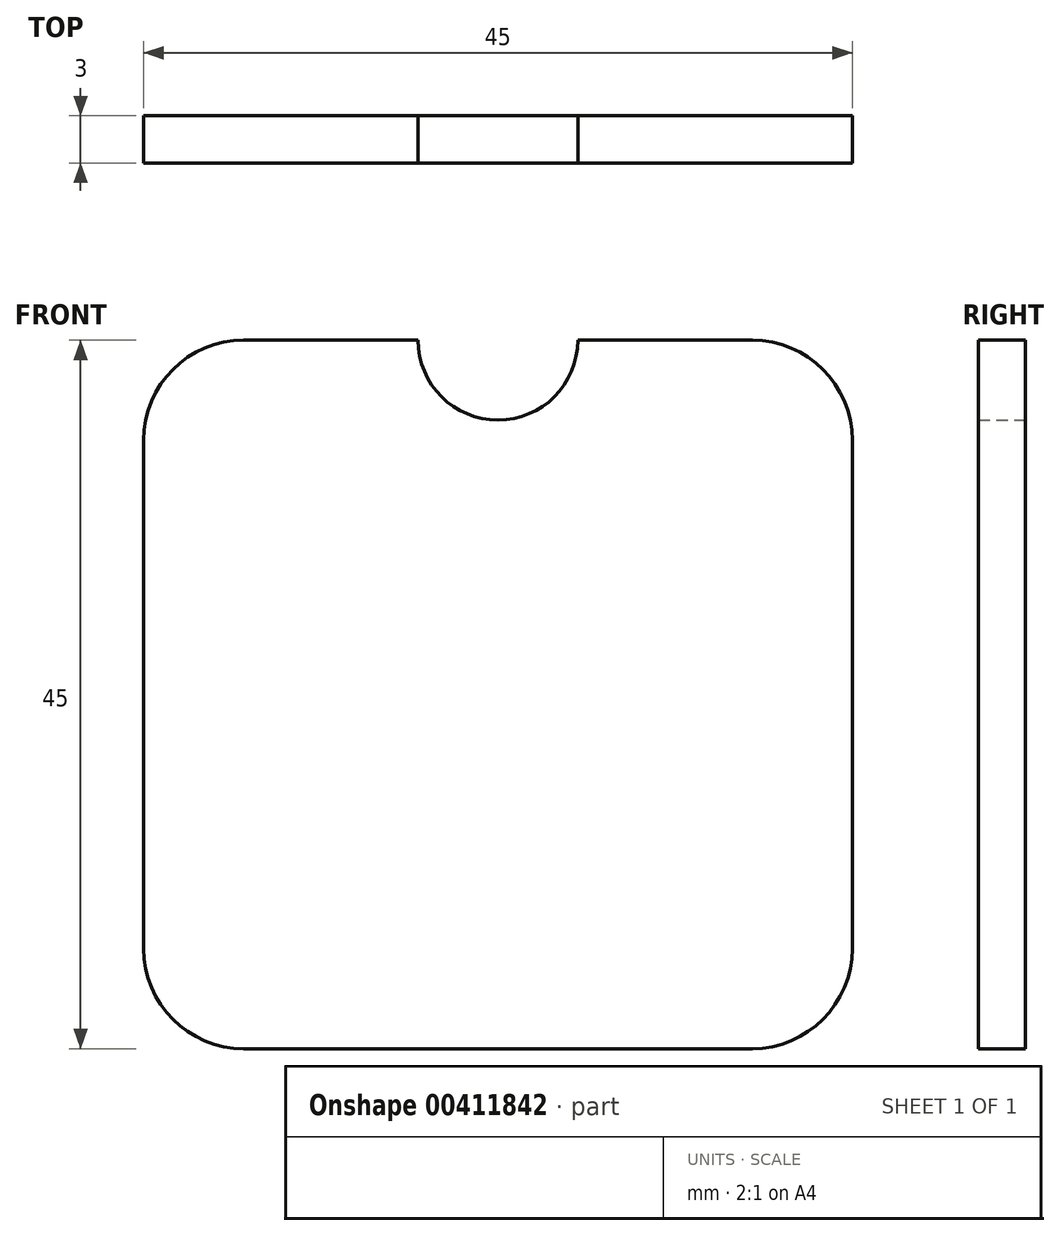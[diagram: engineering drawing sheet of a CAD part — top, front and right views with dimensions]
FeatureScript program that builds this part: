
annotation { "Feature Type Name" : "Feature", "Feature Type Description" : "" }
export const myFeature = defineFeature(function(context is Context, id is Id, definition is map)
    precondition{}
    {
        {
            var Q0;
            Q0=qCreatedBy(makeId("Front.planeOp"),FACE);
            var sketch = newSketch(context, id + "F0", { "sketchPlane" : qUnion([Q0])});
            skLineSegment(sketch, "E0.bottom", {"start": v(16.15, 22.5) * mm, "end": v(-16.15, 22.5) * mm});
            skLineSegment(sketch, "E0.top", {"start": v(16.15, -22.5) * mm, "end": v(-16.15, -22.5) * mm});
            skLineSegment(sketch, "E0.left", {"start": v(22.5, 16.15) * mm, "end": v(22.5, -16.15) * mm});
            skLineSegment(sketch, "E0.right", {"start": v(-22.5, 16.15) * mm, "end": v(-22.5, -16.15) * mm});
            skPoint(sketch, "E0.middle", {"position": v(0, 0) * mm});
            skPoint(sketch, "E1.visualSharp", {"position": v(22.5, 22.5) * mm});
            skArc(sketch, "E1.filletArc", {"start": v(22.5, 16.15) * mm, "mid": v(20.64, 20.64) * mm, "end": v(16.15, 22.5) * mm});
            skPoint(sketch, "E2.visualSharp", {"position": v(22.5, -22.5) * mm});
            skArc(sketch, "E2.filletArc", {"start": v(16.15, -22.5) * mm, "mid": v(20.64, -20.64) * mm, "end": v(22.5, -16.15) * mm});
            skPoint(sketch, "E3.visualSharp", {"position": v(-22.5, 22.5) * mm});
            skArc(sketch, "E3.filletArc", {"start": v(-16.15, 22.5) * mm, "mid": v(-20.64, 20.64) * mm, "end": v(-22.5, 16.15) * mm});
            skPoint(sketch, "E4.visualSharp", {"position": v(-22.5, -22.5) * mm});
            skArc(sketch, "E4.filletArc", {"start": v(-22.5, -16.15) * mm, "mid": v(-20.64, -20.64) * mm, "end": v(-16.15, -22.5) * mm});
            skCircle(sketch, "E5", {"center": v(0, 22.5) * mm, "radius": 5.07 * mm});
            skLineSegment(sketch, "E6.bottom", {"start": v(9, 17.5) * mm, "end": v(-9, 17.5) * mm});
            skLineSegment(sketch, "E6.top", {"start": v(9, -17.5) * mm, "end": v(-9, -17.5) * mm});
            skLineSegment(sketch, "E6.left", {"start": v(9, 17.5) * mm, "end": v(9, -17.5) * mm});
            skLineSegment(sketch, "E6.right", {"start": v(-9, 17.5) * mm, "end": v(-9, -17.5) * mm});
            skSolve(sketch);
        }
        {
            var Q0;
            Q0=makeQuery(id+"F0.imprint","IMPRINT",FACE,{"disambiguationData":[TD([[makeQuery(id+"F0.imprint","IMPRINT",EDGE,{"derivedFrom":sQuery(id+"F0.wireOp",EDGE,"E0.top")}),-1.0]])]});
            var Q1;
            {var subQ0=sQuery(id+"F0.wireOp",EDGE,"E5");var subQ1=sQuery(id+"F0.wireOp",EDGE,"E0.bottom");var subQ2=makeQuery(id+"F0.imprint","INTERSECT",VERTEX,{"disambiguationData":[OD(0.0)],"derivedFrom":[subQ1,subQ0]});Q1=makeQuery(id+"F0.imprint","IMPRINT",FACE,{"disambiguationData":[TD([[makeQuery(id+"F0.imprint","IMPRINT",EDGE,{"disambiguationData":[TD([[subQ2,-1.0]])],"derivedFrom":subQ1}),-1.0]])]});}
            var Q2;
            {var subQ0=sQuery(id+"F0.wireOp",EDGE,"E5");var subQ1=sQuery(id+"F0.wireOp",EDGE,"E0.bottom");var subQ2=makeQuery(id+"F0.imprint","INTERSECT",VERTEX,{"disambiguationData":[OD(0.0)],"derivedFrom":[subQ1,subQ0]});Q2=makeQuery(id+"F0.imprint","IMPRINT",FACE,{"disambiguationData":[TD([[makeQuery(id+"F0.imprint","IMPRINT",EDGE,{"disambiguationData":[TD([[subQ2,-1.0]])],"derivedFrom":subQ1}),1.0]])]});}
            extrude(context, id + "F1", {"entities" : qUnion([Q0, Q1, Q2]), "depth" : 3 * mm, "offsetDistance" : 25.4 * mm});
        }
        {
            var Q0;
            {var subQ0=sQuery(id+"F0.wireOp",EDGE,"E5");var subQ1=sQuery(id+"F0.wireOp",EDGE,"E0.bottom");var subQ2=makeQuery(id+"F0.imprint","INTERSECT",VERTEX,{"disambiguationData":[OD(0.0)],"derivedFrom":[subQ1,subQ0]});Q0=makeQuery(id+"F0.imprint","IMPRINT",FACE,{"disambiguationData":[TD([[makeQuery(id+"F0.imprint","IMPRINT",EDGE,{"disambiguationData":[TD([[subQ2,-1.0]])],"derivedFrom":subQ1}),1.0]])]});}
            var Q1;
            Q1=makeQuery(id+"F0.imprint","IMPRINT",FACE,{"disambiguationData":[TD([[makeQuery(id+"F0.imprint","IMPRINT",EDGE,{"derivedFrom":sQuery(id+"F0.wireOp",EDGE,"E0.top")}),-1.0]])]});
            var Q2;
            Q2=makeQuery(id+"F0.imprint","IMPRINT",FACE,{"disambiguationData":[TD([[makeQuery(id+"F0.imprint","IMPRINT",EDGE,{"derivedFrom":sQuery(id+"F0.wireOp",EDGE,"E6.top")}),-1.0]])]});
            var Q3;
            {var subQ0=sQuery(id+"F0.wireOp",EDGE,"E5");var subQ1=sQuery(id+"F0.wireOp",EDGE,"E0.bottom");var subQ2=makeQuery(id+"F0.imprint","INTERSECT",VERTEX,{"disambiguationData":[OD(0.0)],"derivedFrom":[subQ1,subQ0]});Q3=makeQuery(id+"F0.imprint","IMPRINT",FACE,{"disambiguationData":[TD([[makeQuery(id+"F0.imprint","IMPRINT",EDGE,{"disambiguationData":[TD([[subQ2,-1.0]])],"derivedFrom":subQ1}),-1.0]])]});}
            extrude(context, id + "F2", {"entities" : qUnion([Q0, Q1, Q2, Q3]), "operationType" : NewBodyOperationType.ADD, "depth" : 3 * mm, "offsetDistance" : 25.4 * mm});
        }
    });
